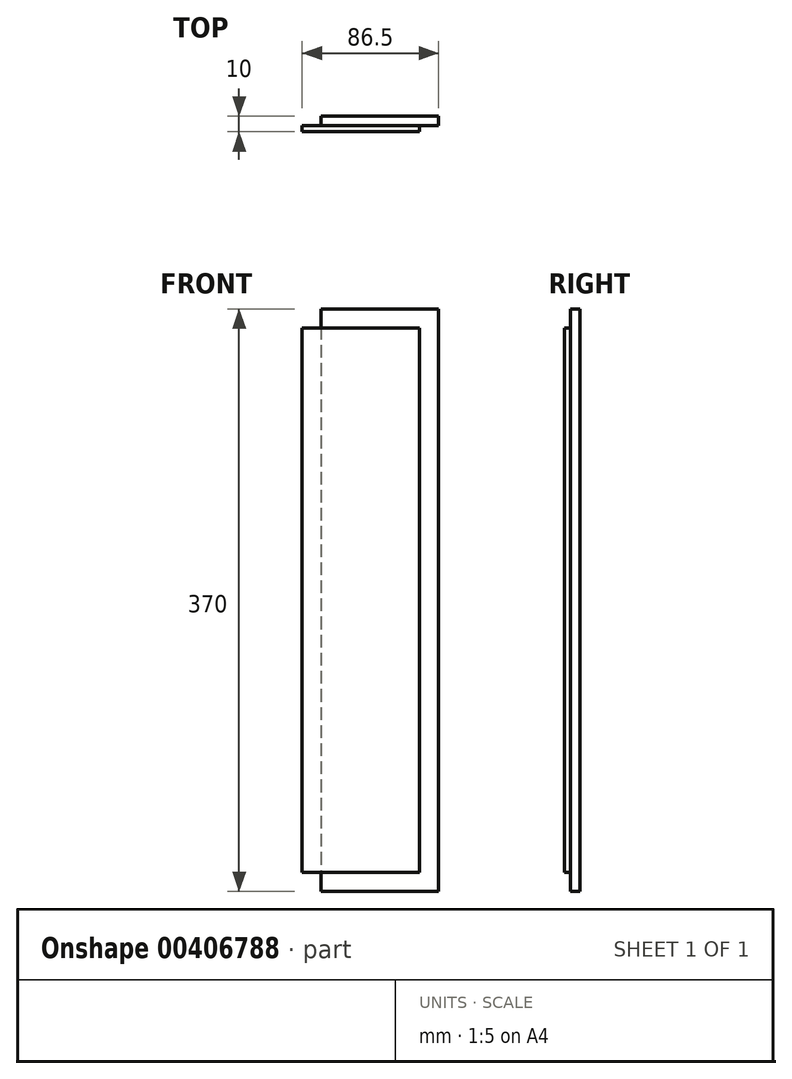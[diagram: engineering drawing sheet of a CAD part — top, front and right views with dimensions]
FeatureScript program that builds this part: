
annotation { "Feature Type Name" : "Feature", "Feature Type Description" : "" }
export const myFeature = defineFeature(function(context is Context, id is Id, definition is map)
    precondition{}
    {
        {
            var Q0;
            Q0=qCreatedBy(makeId("Front.planeOp"),FACE);
            var sketch = newSketch(context, id + "F0", { "sketchPlane" : qUnion([Q0])});
            skLineSegment(sketch, "E0.bottom", {"start": v(43.25, 185) * mm, "end": v(-43.25, 185) * mm});
            skLineSegment(sketch, "E0.top", {"start": v(43.25, -185) * mm, "end": v(-43.25, -185) * mm});
            skLineSegment(sketch, "E0.left", {"start": v(43.25, 185) * mm, "end": v(43.25, -185) * mm});
            skLineSegment(sketch, "E0.right", {"start": v(-43.25, 185) * mm, "end": v(-43.25, -185) * mm});
            skPoint(sketch, "E0.middle", {"position": v(0, 0) * mm});
            skSolve(sketch);
        }
        {
            var Q0;
            Q0=makeQuery(id+"F0.imprint","IMPRINT",FACE,{"disambiguationData":[TD([[makeQuery(id+"F0.imprint","IMPRINT",EDGE,{"derivedFrom":sQuery(id+"F0.wireOp",EDGE,"E0.bottom")}),1.0]])]});
            extrude(context, id + "F1", {"entities" : qUnion([Q0]), "depth" : 10 * mm});
        }
        {
            var Q0;
            Q0=makeQuery(id+"F1.opExtrude","CAP_FACE",FACE,{"disambiguationData":[OSD([sQuery(id+"F0.wireOp",EDGE,"E0.bottom"),sQuery(id+"F0.wireOp",EDGE,"E0.top"),sQuery(id+"F0.wireOp",EDGE,"E0.left"),sQuery(id+"F0.wireOp",EDGE,"E0.right")])],"isStart":false});
            var sketch = newSketch(context, id + "F2", { "sketchPlane" : qUnion([Q0])});
            skLineSegment(sketch, "E1.bottom", {"start": v(-43.25, 173) * mm, "end": v(31.25, 173) * mm});
            skLineSegment(sketch, "E1.top", {"start": v(-43.25, -173) * mm, "end": v(31.25, -173) * mm});
            skLineSegment(sketch, "E1.left", {"start": v(-43.25, 173) * mm, "end": v(-43.25, -173) * mm});
            skLineSegment(sketch, "E1.right", {"start": v(31.25, 173) * mm, "end": v(31.25, -173) * mm});
            skSolve(sketch);
        }
        {
            var Q0;
            {var subQ2=sQuery(id+"F2.wireOp",EDGE,"E1.bottom");Q0=makeQuery(id+"F2.imprint","IMPRINT",FACE,{"disambiguationData":[TD([[makeQuery(id+"F2.imprint","IMPRINT",EDGE,{"derivedFrom":subQ2}),1.0]])]});}
            extrude(context, id + "F3", {"entities" : qUnion([Q0]), "operationType" : NewBodyOperationType.REMOVE, "oppositeDirection" : true, "depth" : 4 * mm});
        }
        {
            var Q0;
            Q0=makeQuery(id+"F1.opExtrude","CAP_FACE",FACE,{"disambiguationData":[OSD([sQuery(id+"F0.wireOp",EDGE,"E0.bottom"),sQuery(id+"F0.wireOp",EDGE,"E0.top"),sQuery(id+"F0.wireOp",EDGE,"E0.left"),sQuery(id+"F0.wireOp",EDGE,"E0.right")])],"isStart":true});
            var sketch = newSketch(context, id + "F4", { "sketchPlane" : qUnion([Q0])});
            skLineSegment(sketch, "E2.bottom", {"start": v(43.25, 185) * mm, "end": v(31.25, 185) * mm});
            skLineSegment(sketch, "E2.top", {"start": v(43.25, -185) * mm, "end": v(31.25, -185) * mm});
            skLineSegment(sketch, "E2.left", {"start": v(43.25, 185) * mm, "end": v(43.25, -185) * mm});
            skLineSegment(sketch, "E2.right", {"start": v(31.25, 185) * mm, "end": v(31.25, -185) * mm});
            skSolve(sketch);
        }
        {
            var Q0;
            Q0 = qSketchRegion(id + "F4", true);
            extrude(context, id + "F5", {"entities" : qUnion([Q0]), "operationType" : NewBodyOperationType.REMOVE, "oppositeDirection" : true, "depth" : 6 * mm});
        }
    });
